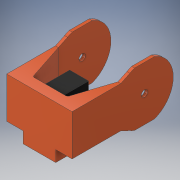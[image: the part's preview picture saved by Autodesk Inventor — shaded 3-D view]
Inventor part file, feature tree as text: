
AUTODESK INVENTOR PART (.ipt)
format: ipt  version: 2017 (Build 210142000, 142)  size: 210,432 bytes
history: native  units: in
note: dims shown in document units (in); Inventor stores cm internally (conversion verified against a paired STEP export)
features: sketch x9, extrude x8, plane x7, fillet x2, mirror x1
ambient origin geometry x8: Origin, YZ Plane, XZ Plane, XY Plane, X Axis, Y Axis, Z Axis, Center Point
bodies: Solid1 (feature_tree)
feature tree (27):
  extrude  "Extrusion1"  Depth=1.7323in
  plane  "Work Plane2"
  extrude  "Extrusion2"  Depth=1.7323in TaperAngle=0.0deg
  plane  "Work Plane4"
  extrude  "Extrusion3"  Depth=0.0787in
  fillet  "Fillet1"  Radius=0.0787in
  fillet  "Fillet2"  Radius=1.9094in
  sketch  "Sketch7"  dims[d25=0.2165in d29=0.0984in d30=0.0in]
  plane  "Work Plane6"
  extrude  "Extrusion4"  Depth=0.0984in TaperAngle=0.0deg
  mirror  "Mirror1"
  sketch  "Sketch14"  dims[d47=0.1969in d48=0.0in d49=0.6299in]
  plane  "Work Plane11"
  extrude  "Extrusion8"  Depth=0.0984in TaperAngle=0.0deg
  plane  "Work Plane7"
  extrude  "Extrusion5"  Depth=1.4961in TaperAngle=0.0deg
  plane  "Work Plane8"
  extrude  "Extrusion6"  Depth=0.5906in
  plane  "Work Plane10"
  extrude  "Extrusion7"  Depth=0.6299in
  sketch  "Sketch1"  dims[d0=2.1654in d1=1.7323in]
  sketch  "Sketch4"  dims[d2=1.6142in d3=0.0in d8=1.7323in d9=0.0in]
  sketch  "Sketch6"  dims[d17=1.7323in d18=0.0in d19=0.0787in d20=0.0787in d22=1.9094in]
  sketch  "Sketch10"  dims[d35=0.2165in d36=0.0984in d37=0.0in]
  sketch  "Sketch11"  dims[d39=0.1969in d40=1.4961in d41=0.0in]
  sketch  "Sketch13"  dims[d45=0.5906in d46=0.5906in]
  sketch  "Sketch15"  dims[d50=0.9646in d51=0.0in]
